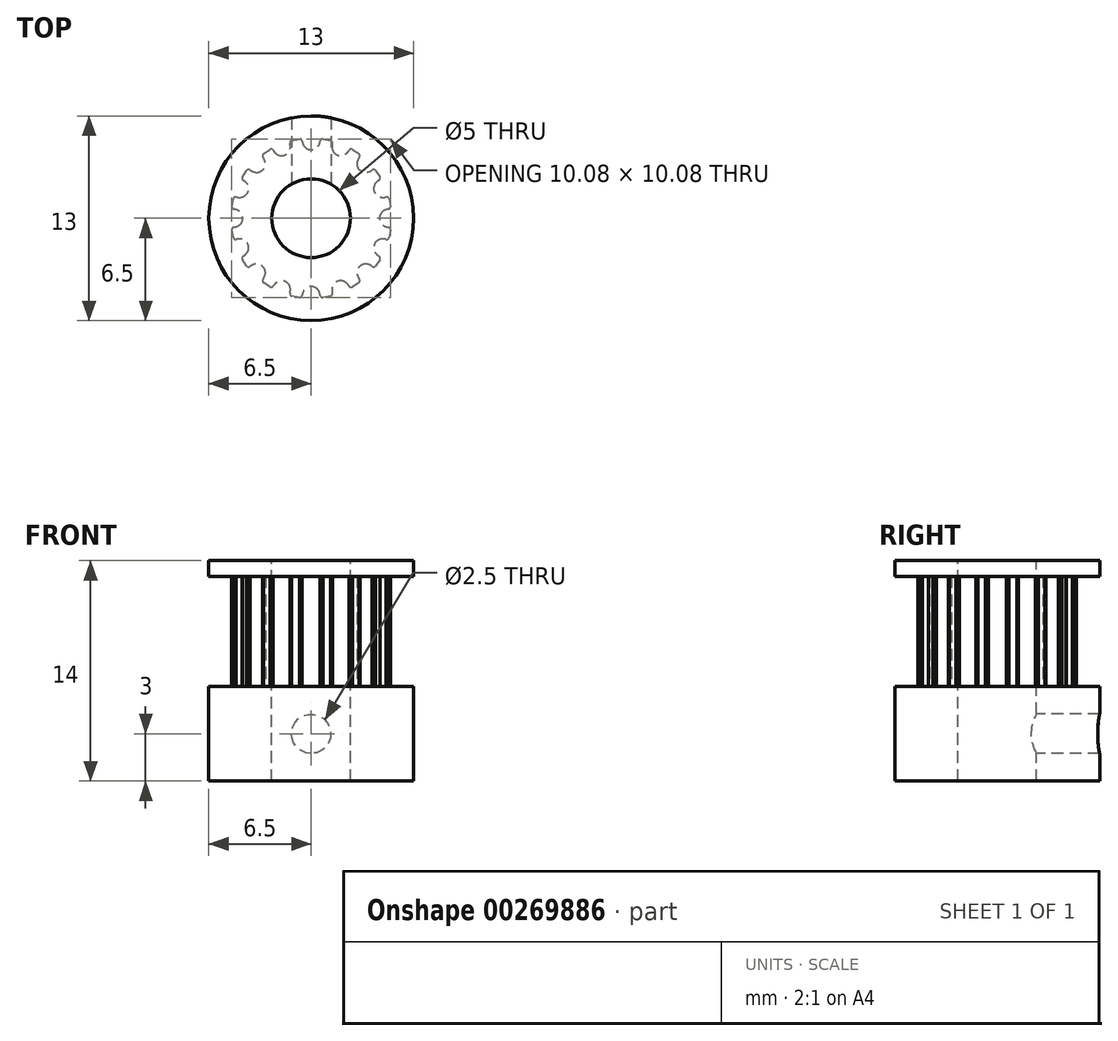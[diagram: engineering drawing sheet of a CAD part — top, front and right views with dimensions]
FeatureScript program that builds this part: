
annotation { "Feature Type Name" : "Feature", "Feature Type Description" : "" }
export const myFeature = defineFeature(function(context is Context, id is Id, definition is map)
    precondition{}
    {
        {
            var Q0;
            Q0=qCreatedBy(makeId("Top.planeOp"),FACE);
            var sketch = newSketch(context, id + "F0", { "sketchPlane" : qUnion([Q0])});
            skLineSegment(sketch, "E0", {"start": v(0, 0) * mm, "end": v(8.05, 0) * mm, "construction": true});
            skArc(sketch, "E1", {"start": v(5.1, 0) * mm, "mid": v(5, 1) * mm, "end": v(4.7, 1.95) * mm, "construction": true});
            skLineSegment(sketch, "E2", {"start": v(0, 0) * mm, "end": v(4.7, 1.95) * mm, "construction": true});
            skPoint(sketch, "E3", {"position": v(4.34, 0) * mm});
            skPoint(sketch, "E4", {"position": v(4.9, 0) * mm});
            skArc(sketch, "E5", {"start": v(4.68, 0.5) * mm, "mid": v(4.34, 0) * mm, "end": v(4.68, -0.5) * mm});
            skArc(sketch, "E6", {"start": v(4.9, 0.58) * mm, "mid": v(4.79, 0.55) * mm, "end": v(4.68, 0.5) * mm});
            skArc(sketch, "E7", {"start": v(4.94, 0) * mm, "mid": v(4.85, 0.96) * mm, "end": v(4.57, 1.9) * mm, "construction": true});
            skArc(sketch, "E8", {"start": v(4.9, 0.58) * mm, "mid": v(5, 0.64) * mm, "end": v(5.04, 0.75) * mm});
            skArc(sketch, "E9", {"start": v(4.97, -1.1) * mm, "mid": v(5.06, -0.56) * mm, "end": v(5.1, 0) * mm, "construction": true});
            skLineSegment(sketch, "E10", {"start": v(0, 0) * mm, "end": v(5, 1) * mm, "construction": true});
            skPoint(sketch, "E11", {"position": v(5, 1) * mm});
            skArc(sketch, "E12.MirrorCS", {"start": v(4.76, 1.34) * mm, "mid": v(4.87, 1.33) * mm, "end": v(4.94, 1.24) * mm});
            skArc(sketch, "E13.MirrorCS", {"start": v(4.76, 1.34) * mm, "mid": v(4.64, 1.32) * mm, "end": v(4.51, 1.32) * mm});
            skArc(sketch, "E14.MirrorCS", {"start": v(4.51, 1.32) * mm, "mid": v(4.01, 1.66) * mm, "end": v(4.12, 2.26) * mm});
            skLineSegment(sketch, "E15", {"start": v(4.94, 1.24) * mm, "end": v(5.04, 0.75) * mm});
            skArc(sketch, "E16.1.0", {"start": v(4.12, 2.26) * mm, "mid": v(4.01, 1.66) * mm, "end": v(4.51, 1.32) * mm});
            skArc(sketch, "E16.1.1", {"start": v(4.31, 2.41) * mm, "mid": v(4.21, 2.34) * mm, "end": v(4.12, 2.26) * mm});
            skArc(sketch, "E16.1.2", {"start": v(4.31, 2.41) * mm, "mid": v(4.38, 2.5) * mm, "end": v(4.37, 2.62) * mm});
            skLineSegment(sketch, "E16.1.3", {"start": v(4.1, 3.03) * mm, "end": v(4.37, 2.62) * mm});
            skArc(sketch, "E16.1.4", {"start": v(3.88, 3.06) * mm, "mid": v(4, 3.1) * mm, "end": v(4.1, 3.03) * mm});
            skArc(sketch, "E16.1.5", {"start": v(3.88, 3.06) * mm, "mid": v(3.78, 3) * mm, "end": v(3.67, 2.95) * mm});
            skArc(sketch, "E16.2.0", {"start": v(2.95, 3.67) * mm, "mid": v(3.07, 3.07) * mm, "end": v(3.67, 2.95) * mm});
            skArc(sketch, "E16.2.1", {"start": v(3.06, 3.88) * mm, "mid": v(3, 3.78) * mm, "end": v(2.95, 3.67) * mm});
            skArc(sketch, "E16.2.2", {"start": v(3.06, 3.88) * mm, "mid": v(3.1, 4) * mm, "end": v(3.03, 4.1) * mm});
            skLineSegment(sketch, "E16.2.3", {"start": v(2.62, 4.37) * mm, "end": v(3.03, 4.1) * mm});
            skArc(sketch, "E16.2.4", {"start": v(2.41, 4.31) * mm, "mid": v(2.5, 4.38) * mm, "end": v(2.62, 4.37) * mm});
            skArc(sketch, "E16.2.5", {"start": v(2.41, 4.31) * mm, "mid": v(2.34, 4.21) * mm, "end": v(2.26, 4.12) * mm});
            skArc(sketch, "E16.3.0", {"start": v(1.32, 4.51) * mm, "mid": v(1.66, 4.01) * mm, "end": v(2.26, 4.12) * mm});
            skArc(sketch, "E16.3.1", {"start": v(1.34, 4.76) * mm, "mid": v(1.32, 4.64) * mm, "end": v(1.32, 4.51) * mm});
            skArc(sketch, "E16.3.2", {"start": v(1.34, 4.76) * mm, "mid": v(1.33, 4.87) * mm, "end": v(1.24, 4.94) * mm});
            skLineSegment(sketch, "E16.3.3", {"start": v(0.75, 5.04) * mm, "end": v(1.24, 4.94) * mm});
            skArc(sketch, "E16.3.4", {"start": v(0.58, 4.9) * mm, "mid": v(0.64, 5) * mm, "end": v(0.75, 5.04) * mm});
            skArc(sketch, "E16.3.5", {"start": v(0.58, 4.9) * mm, "mid": v(0.55, 4.79) * mm, "end": v(0.5, 4.68) * mm});
            skArc(sketch, "E16.4.0", {"start": v(-0.5, 4.68) * mm, "mid": v(0, 4.34) * mm, "end": v(0.5, 4.68) * mm});
            skArc(sketch, "E16.4.1", {"start": v(-0.58, 4.9) * mm, "mid": v(-0.55, 4.79) * mm, "end": v(-0.5, 4.68) * mm});
            skArc(sketch, "E16.4.2", {"start": v(-0.58, 4.9) * mm, "mid": v(-0.64, 5) * mm, "end": v(-0.75, 5.04) * mm});
            skLineSegment(sketch, "E16.4.3", {"start": v(-1.24, 4.94) * mm, "end": v(-0.75, 5.04) * mm});
            skArc(sketch, "E16.4.4", {"start": v(-1.34, 4.76) * mm, "mid": v(-1.33, 4.87) * mm, "end": v(-1.24, 4.94) * mm});
            skArc(sketch, "E16.4.5", {"start": v(-1.34, 4.76) * mm, "mid": v(-1.32, 4.64) * mm, "end": v(-1.32, 4.51) * mm});
            skArc(sketch, "E16.5.0", {"start": v(-2.26, 4.12) * mm, "mid": v(-1.66, 4.01) * mm, "end": v(-1.32, 4.51) * mm});
            skArc(sketch, "E16.5.1", {"start": v(-2.41, 4.31) * mm, "mid": v(-2.34, 4.21) * mm, "end": v(-2.26, 4.12) * mm});
            skArc(sketch, "E16.5.2", {"start": v(-2.41, 4.31) * mm, "mid": v(-2.5, 4.38) * mm, "end": v(-2.62, 4.37) * mm});
            skLineSegment(sketch, "E16.5.3", {"start": v(-3.03, 4.1) * mm, "end": v(-2.62, 4.37) * mm});
            skArc(sketch, "E16.5.4", {"start": v(-3.06, 3.88) * mm, "mid": v(-3.1, 4) * mm, "end": v(-3.03, 4.1) * mm});
            skArc(sketch, "E16.5.5", {"start": v(-3.06, 3.88) * mm, "mid": v(-3, 3.78) * mm, "end": v(-2.95, 3.67) * mm});
            skArc(sketch, "E16.6.0", {"start": v(-3.67, 2.95) * mm, "mid": v(-3.07, 3.07) * mm, "end": v(-2.95, 3.67) * mm});
            skArc(sketch, "E16.6.1", {"start": v(-3.88, 3.06) * mm, "mid": v(-3.78, 3) * mm, "end": v(-3.67, 2.95) * mm});
            skArc(sketch, "E16.6.2", {"start": v(-3.88, 3.06) * mm, "mid": v(-4, 3.1) * mm, "end": v(-4.1, 3.03) * mm});
            skLineSegment(sketch, "E16.6.3", {"start": v(-4.37, 2.62) * mm, "end": v(-4.1, 3.03) * mm});
            skArc(sketch, "E16.6.4", {"start": v(-4.31, 2.41) * mm, "mid": v(-4.38, 2.5) * mm, "end": v(-4.37, 2.62) * mm});
            skArc(sketch, "E16.6.5", {"start": v(-4.31, 2.41) * mm, "mid": v(-4.21, 2.34) * mm, "end": v(-4.12, 2.26) * mm});
            skArc(sketch, "E16.7.0", {"start": v(-4.51, 1.32) * mm, "mid": v(-4.01, 1.66) * mm, "end": v(-4.12, 2.26) * mm});
            skArc(sketch, "E16.7.1", {"start": v(-4.76, 1.34) * mm, "mid": v(-4.64, 1.32) * mm, "end": v(-4.51, 1.32) * mm});
            skArc(sketch, "E16.7.2", {"start": v(-4.76, 1.34) * mm, "mid": v(-4.87, 1.33) * mm, "end": v(-4.94, 1.24) * mm});
            skLineSegment(sketch, "E16.7.3", {"start": v(-5.04, 0.75) * mm, "end": v(-4.94, 1.24) * mm});
            skArc(sketch, "E16.7.4", {"start": v(-4.9, 0.58) * mm, "mid": v(-5, 0.64) * mm, "end": v(-5.04, 0.75) * mm});
            skArc(sketch, "E16.7.5", {"start": v(-4.9, 0.58) * mm, "mid": v(-4.79, 0.55) * mm, "end": v(-4.68, 0.5) * mm});
            skArc(sketch, "E16.8.0", {"start": v(-4.68, -0.5) * mm, "mid": v(-4.34, 0) * mm, "end": v(-4.68, 0.5) * mm});
            skArc(sketch, "E16.8.1", {"start": v(-4.9, -0.58) * mm, "mid": v(-4.79, -0.55) * mm, "end": v(-4.68, -0.5) * mm});
            skArc(sketch, "E16.8.2", {"start": v(-4.9, -0.58) * mm, "mid": v(-5, -0.64) * mm, "end": v(-5.04, -0.75) * mm});
            skLineSegment(sketch, "E16.8.3", {"start": v(-4.94, -1.24) * mm, "end": v(-5.04, -0.75) * mm});
            skArc(sketch, "E16.8.4", {"start": v(-4.76, -1.34) * mm, "mid": v(-4.87, -1.33) * mm, "end": v(-4.94, -1.24) * mm});
            skArc(sketch, "E16.8.5", {"start": v(-4.76, -1.34) * mm, "mid": v(-4.64, -1.32) * mm, "end": v(-4.51, -1.32) * mm});
            skArc(sketch, "E16.9.0", {"start": v(-4.12, -2.26) * mm, "mid": v(-4.01, -1.66) * mm, "end": v(-4.51, -1.32) * mm});
            skArc(sketch, "E16.9.1", {"start": v(-4.31, -2.41) * mm, "mid": v(-4.21, -2.34) * mm, "end": v(-4.12, -2.26) * mm});
            skArc(sketch, "E16.9.2", {"start": v(-4.31, -2.41) * mm, "mid": v(-4.38, -2.5) * mm, "end": v(-4.37, -2.62) * mm});
            skLineSegment(sketch, "E16.9.3", {"start": v(-4.1, -3.03) * mm, "end": v(-4.37, -2.62) * mm});
            skArc(sketch, "E16.9.4", {"start": v(-3.88, -3.06) * mm, "mid": v(-4, -3.1) * mm, "end": v(-4.1, -3.03) * mm});
            skArc(sketch, "E16.9.5", {"start": v(-3.88, -3.06) * mm, "mid": v(-3.78, -3) * mm, "end": v(-3.67, -2.95) * mm});
            skArc(sketch, "E16.10.0", {"start": v(-2.95, -3.67) * mm, "mid": v(-3.07, -3.07) * mm, "end": v(-3.67, -2.95) * mm});
            skArc(sketch, "E16.10.1", {"start": v(-3.06, -3.88) * mm, "mid": v(-3, -3.78) * mm, "end": v(-2.95, -3.67) * mm});
            skArc(sketch, "E16.10.2", {"start": v(-3.06, -3.88) * mm, "mid": v(-3.1, -4) * mm, "end": v(-3.03, -4.1) * mm});
            skLineSegment(sketch, "E16.10.3", {"start": v(-2.62, -4.37) * mm, "end": v(-3.03, -4.1) * mm});
            skArc(sketch, "E16.10.4", {"start": v(-2.41, -4.31) * mm, "mid": v(-2.5, -4.38) * mm, "end": v(-2.62, -4.37) * mm});
            skArc(sketch, "E16.10.5", {"start": v(-2.41, -4.31) * mm, "mid": v(-2.34, -4.21) * mm, "end": v(-2.26, -4.12) * mm});
            skArc(sketch, "E16.11.0", {"start": v(-1.32, -4.51) * mm, "mid": v(-1.66, -4.01) * mm, "end": v(-2.26, -4.12) * mm});
            skArc(sketch, "E16.11.1", {"start": v(-1.34, -4.76) * mm, "mid": v(-1.32, -4.64) * mm, "end": v(-1.32, -4.51) * mm});
            skArc(sketch, "E16.11.2", {"start": v(-1.34, -4.76) * mm, "mid": v(-1.33, -4.87) * mm, "end": v(-1.24, -4.94) * mm});
            skLineSegment(sketch, "E16.11.3", {"start": v(-0.75, -5.04) * mm, "end": v(-1.24, -4.94) * mm});
            skArc(sketch, "E16.11.4", {"start": v(-0.58, -4.9) * mm, "mid": v(-0.64, -5) * mm, "end": v(-0.75, -5.04) * mm});
            skArc(sketch, "E16.11.5", {"start": v(-0.58, -4.9) * mm, "mid": v(-0.55, -4.79) * mm, "end": v(-0.5, -4.68) * mm});
            skArc(sketch, "E16.12.0", {"start": v(0.5, -4.68) * mm, "mid": v(0, -4.34) * mm, "end": v(-0.5, -4.68) * mm});
            skArc(sketch, "E16.12.1", {"start": v(0.58, -4.9) * mm, "mid": v(0.55, -4.79) * mm, "end": v(0.5, -4.68) * mm});
            skArc(sketch, "E16.12.2", {"start": v(0.58, -4.9) * mm, "mid": v(0.64, -5) * mm, "end": v(0.75, -5.04) * mm});
            skLineSegment(sketch, "E16.12.3", {"start": v(1.24, -4.94) * mm, "end": v(0.75, -5.04) * mm});
            skArc(sketch, "E16.12.4", {"start": v(1.34, -4.76) * mm, "mid": v(1.33, -4.87) * mm, "end": v(1.24, -4.94) * mm});
            skArc(sketch, "E16.12.5", {"start": v(1.34, -4.76) * mm, "mid": v(1.32, -4.64) * mm, "end": v(1.32, -4.51) * mm});
            skArc(sketch, "E16.13.0", {"start": v(2.26, -4.12) * mm, "mid": v(1.66, -4.01) * mm, "end": v(1.32, -4.51) * mm});
            skArc(sketch, "E16.13.1", {"start": v(2.41, -4.31) * mm, "mid": v(2.34, -4.21) * mm, "end": v(2.26, -4.12) * mm});
            skArc(sketch, "E16.13.2", {"start": v(2.41, -4.31) * mm, "mid": v(2.5, -4.38) * mm, "end": v(2.62, -4.37) * mm});
            skLineSegment(sketch, "E16.13.3", {"start": v(3.03, -4.1) * mm, "end": v(2.62, -4.37) * mm});
            skArc(sketch, "E16.13.4", {"start": v(3.06, -3.88) * mm, "mid": v(3.1, -4) * mm, "end": v(3.03, -4.1) * mm});
            skArc(sketch, "E16.13.5", {"start": v(3.06, -3.88) * mm, "mid": v(3, -3.78) * mm, "end": v(2.95, -3.67) * mm});
            skArc(sketch, "E16.14.0", {"start": v(3.67, -2.95) * mm, "mid": v(3.07, -3.07) * mm, "end": v(2.95, -3.67) * mm});
            skArc(sketch, "E16.14.1", {"start": v(3.88, -3.06) * mm, "mid": v(3.78, -3) * mm, "end": v(3.67, -2.95) * mm});
            skArc(sketch, "E16.14.2", {"start": v(3.88, -3.06) * mm, "mid": v(4, -3.1) * mm, "end": v(4.1, -3.03) * mm});
            skLineSegment(sketch, "E16.14.3", {"start": v(4.37, -2.62) * mm, "end": v(4.1, -3.03) * mm});
            skArc(sketch, "E16.14.4", {"start": v(4.31, -2.41) * mm, "mid": v(4.38, -2.5) * mm, "end": v(4.37, -2.62) * mm});
            skArc(sketch, "E16.14.5", {"start": v(4.31, -2.41) * mm, "mid": v(4.21, -2.34) * mm, "end": v(4.12, -2.26) * mm});
            skArc(sketch, "E16.15.0", {"start": v(4.51, -1.32) * mm, "mid": v(4.01, -1.66) * mm, "end": v(4.12, -2.26) * mm});
            skArc(sketch, "E16.15.1", {"start": v(4.76, -1.34) * mm, "mid": v(4.64, -1.32) * mm, "end": v(4.51, -1.32) * mm});
            skArc(sketch, "E16.15.2", {"start": v(4.76, -1.34) * mm, "mid": v(4.87, -1.33) * mm, "end": v(4.94, -1.24) * mm});
            skLineSegment(sketch, "E16.15.3", {"start": v(5.04, -0.75) * mm, "end": v(4.94, -1.24) * mm});
            skArc(sketch, "E16.15.4", {"start": v(4.9, -0.58) * mm, "mid": v(5, -0.64) * mm, "end": v(5.04, -0.75) * mm});
            skArc(sketch, "E16.15.5", {"start": v(4.9, -0.58) * mm, "mid": v(4.79, -0.55) * mm, "end": v(4.68, -0.5) * mm});
            skCircle(sketch, "E17", {"center": v(0, 0) * mm, "radius": 2.5 * mm});
            skCircle(sketch, "E18", {"center": v(0, 0) * mm, "radius": 6.5 * mm});
            skSolve(sketch);
        }
        {
            var Q0;
            Q0=makeQuery(id+"F0.imprint","IMPRINT",FACE,{"disambiguationData":[TD([[makeQuery(id+"F0.imprint","IMPRINT",EDGE,{"derivedFrom":sQuery(id+"F0.wireOp",EDGE,"E5")}),-1.0]])]});
            var Q1;
            Q1=makeQuery(id+"F0.imprint","IMPRINT",FACE,{"disambiguationData":[TD([[makeQuery(id+"F0.imprint","IMPRINT",EDGE,{"derivedFrom":sQuery(id+"F0.wireOp",EDGE,"E5")}),1.0]])]});
            extrude(context, id + "F1", {"entities" : qUnion([Q0, Q1]), "oppositeDirection" : true, "depth" : 6 * mm});
        }
        {
            var Q0;
            Q0=makeQuery(id+"F0.imprint","IMPRINT",FACE,{"disambiguationData":[TD([[makeQuery(id+"F0.imprint","IMPRINT",EDGE,{"derivedFrom":sQuery(id+"F0.wireOp",EDGE,"E5")}),-1.0]])]});
            extrude(context, id + "F2", {"entities" : qUnion([Q0]), "operationType" : NewBodyOperationType.ADD, "depth" : 7 * mm});
        }
        {
            var Q0;
            Q0=makeQuery(id+"F0.imprint","IMPRINT",FACE,{"disambiguationData":[TD([[makeQuery(id+"F0.imprint","IMPRINT",EDGE,{"derivedFrom":sQuery(id+"F0.wireOp",EDGE,"E5")}),1.0]])]});
            var Q1;
            Q1=makeQuery(id+"F0.imprint","IMPRINT",FACE,{"disambiguationData":[TD([[makeQuery(id+"F0.imprint","IMPRINT",EDGE,{"derivedFrom":sQuery(id+"F0.wireOp",EDGE,"E5")}),-1.0]])]});
            var Q2;
            Q2=makeQuery(id+"F2.opExtrude","CAP_FACE",FACE,{"disambiguationData":[OSD([sQuery(id+"F0.wireOp",EDGE,"E5"),sQuery(id+"F0.wireOp",EDGE,"E6"),sQuery(id+"F0.wireOp",EDGE,"E8"),sQuery(id+"F0.wireOp",EDGE,"E12.MirrorCS"),sQuery(id+"F0.wireOp",EDGE,"E13.MirrorCS"),sQuery(id+"F0.wireOp",EDGE,"E15"),sQuery(id+"F0.wireOp",EDGE,"E16.1.0"),sQuery(id+"F0.wireOp",EDGE,"E16.1.1"),sQuery(id+"F0.wireOp",EDGE,"E16.1.2"),sQuery(id+"F0.wireOp",EDGE,"E16.1.3"),sQuery(id+"F0.wireOp",EDGE,"E16.1.4"),sQuery(id+"F0.wireOp",EDGE,"E16.1.5"),sQuery(id+"F0.wireOp",EDGE,"E16.2.0"),sQuery(id+"F0.wireOp",EDGE,"E16.2.1"),sQuery(id+"F0.wireOp",EDGE,"E16.2.2"),sQuery(id+"F0.wireOp",EDGE,"E16.2.3"),sQuery(id+"F0.wireOp",EDGE,"E16.2.4"),sQuery(id+"F0.wireOp",EDGE,"E16.2.5"),sQuery(id+"F0.wireOp",EDGE,"E16.3.0"),sQuery(id+"F0.wireOp",EDGE,"E16.3.1"),sQuery(id+"F0.wireOp",EDGE,"E16.3.2"),sQuery(id+"F0.wireOp",EDGE,"E16.3.3"),sQuery(id+"F0.wireOp",EDGE,"E16.3.4"),sQuery(id+"F0.wireOp",EDGE,"E16.3.5"),sQuery(id+"F0.wireOp",EDGE,"E16.4.0"),sQuery(id+"F0.wireOp",EDGE,"E16.4.1"),sQuery(id+"F0.wireOp",EDGE,"E16.4.2"),sQuery(id+"F0.wireOp",EDGE,"E16.4.3"),sQuery(id+"F0.wireOp",EDGE,"E16.4.4"),sQuery(id+"F0.wireOp",EDGE,"E16.4.5"),sQuery(id+"F0.wireOp",EDGE,"E16.5.0"),sQuery(id+"F0.wireOp",EDGE,"E16.5.1"),sQuery(id+"F0.wireOp",EDGE,"E16.5.2"),sQuery(id+"F0.wireOp",EDGE,"E16.5.3"),sQuery(id+"F0.wireOp",EDGE,"E16.5.4"),sQuery(id+"F0.wireOp",EDGE,"E16.5.5"),sQuery(id+"F0.wireOp",EDGE,"E16.6.0"),sQuery(id+"F0.wireOp",EDGE,"E16.6.1"),sQuery(id+"F0.wireOp",EDGE,"E16.6.2"),sQuery(id+"F0.wireOp",EDGE,"E16.6.3"),sQuery(id+"F0.wireOp",EDGE,"E16.6.4"),sQuery(id+"F0.wireOp",EDGE,"E16.6.5"),sQuery(id+"F0.wireOp",EDGE,"E16.7.0"),sQuery(id+"F0.wireOp",EDGE,"E16.7.1"),sQuery(id+"F0.wireOp",EDGE,"E16.7.2"),sQuery(id+"F0.wireOp",EDGE,"E16.7.3"),sQuery(id+"F0.wireOp",EDGE,"E16.7.4"),sQuery(id+"F0.wireOp",EDGE,"E16.7.5"),sQuery(id+"F0.wireOp",EDGE,"E16.8.0"),sQuery(id+"F0.wireOp",EDGE,"E16.8.1"),sQuery(id+"F0.wireOp",EDGE,"E16.8.2"),sQuery(id+"F0.wireOp",EDGE,"E16.8.3"),sQuery(id+"F0.wireOp",EDGE,"E16.8.4"),sQuery(id+"F0.wireOp",EDGE,"E16.8.5"),sQuery(id+"F0.wireOp",EDGE,"E16.9.0"),sQuery(id+"F0.wireOp",EDGE,"E16.9.1"),sQuery(id+"F0.wireOp",EDGE,"E16.9.2"),sQuery(id+"F0.wireOp",EDGE,"E16.9.3"),sQuery(id+"F0.wireOp",EDGE,"E16.9.4"),sQuery(id+"F0.wireOp",EDGE,"E16.9.5"),sQuery(id+"F0.wireOp",EDGE,"E16.10.0"),sQuery(id+"F0.wireOp",EDGE,"E16.10.1"),sQuery(id+"F0.wireOp",EDGE,"E16.10.2"),sQuery(id+"F0.wireOp",EDGE,"E16.10.3"),sQuery(id+"F0.wireOp",EDGE,"E16.10.4"),sQuery(id+"F0.wireOp",EDGE,"E16.10.5"),sQuery(id+"F0.wireOp",EDGE,"E16.11.0"),sQuery(id+"F0.wireOp",EDGE,"E16.11.1"),sQuery(id+"F0.wireOp",EDGE,"E16.11.2"),sQuery(id+"F0.wireOp",EDGE,"E16.11.3"),sQuery(id+"F0.wireOp",EDGE,"E16.11.4"),sQuery(id+"F0.wireOp",EDGE,"E16.11.5"),sQuery(id+"F0.wireOp",EDGE,"E16.12.0"),sQuery(id+"F0.wireOp",EDGE,"E16.12.1"),sQuery(id+"F0.wireOp",EDGE,"E16.12.2"),sQuery(id+"F0.wireOp",EDGE,"E16.12.3"),sQuery(id+"F0.wireOp",EDGE,"E16.12.4"),sQuery(id+"F0.wireOp",EDGE,"E16.12.5"),sQuery(id+"F0.wireOp",EDGE,"E16.13.0"),sQuery(id+"F0.wireOp",EDGE,"E16.13.1"),sQuery(id+"F0.wireOp",EDGE,"E16.13.2"),sQuery(id+"F0.wireOp",EDGE,"E16.13.3"),sQuery(id+"F0.wireOp",EDGE,"E16.13.4"),sQuery(id+"F0.wireOp",EDGE,"E16.13.5"),sQuery(id+"F0.wireOp",EDGE,"E16.14.0"),sQuery(id+"F0.wireOp",EDGE,"E16.14.1"),sQuery(id+"F0.wireOp",EDGE,"E16.14.2"),sQuery(id+"F0.wireOp",EDGE,"E16.14.3"),sQuery(id+"F0.wireOp",EDGE,"E16.14.4"),sQuery(id+"F0.wireOp",EDGE,"E16.14.5"),sQuery(id+"F0.wireOp",EDGE,"E16.15.0"),sQuery(id+"F0.wireOp",EDGE,"E16.15.1"),sQuery(id+"F0.wireOp",EDGE,"E16.15.2"),sQuery(id+"F0.wireOp",EDGE,"E16.15.3"),sQuery(id+"F0.wireOp",EDGE,"E16.15.4"),sQuery(id+"F0.wireOp",EDGE,"E16.15.5"),sQuery(id+"F0.wireOp",EDGE,"E17")])],"isStart":false});
            var Q3;
            Q3=makeQuery(id+"F2.opExtrude","CAP_FACE",FACE,{"disambiguationData":[OSD([sQuery(id+"F0.wireOp",EDGE,"E5"),sQuery(id+"F0.wireOp",EDGE,"E6"),sQuery(id+"F0.wireOp",EDGE,"E8"),sQuery(id+"F0.wireOp",EDGE,"E12.MirrorCS"),sQuery(id+"F0.wireOp",EDGE,"E13.MirrorCS"),sQuery(id+"F0.wireOp",EDGE,"E15"),sQuery(id+"F0.wireOp",EDGE,"E16.1.0"),sQuery(id+"F0.wireOp",EDGE,"E16.1.1"),sQuery(id+"F0.wireOp",EDGE,"E16.1.2"),sQuery(id+"F0.wireOp",EDGE,"E16.1.3"),sQuery(id+"F0.wireOp",EDGE,"E16.1.4"),sQuery(id+"F0.wireOp",EDGE,"E16.1.5"),sQuery(id+"F0.wireOp",EDGE,"E16.2.0"),sQuery(id+"F0.wireOp",EDGE,"E16.2.1"),sQuery(id+"F0.wireOp",EDGE,"E16.2.2"),sQuery(id+"F0.wireOp",EDGE,"E16.2.3"),sQuery(id+"F0.wireOp",EDGE,"E16.2.4"),sQuery(id+"F0.wireOp",EDGE,"E16.2.5"),sQuery(id+"F0.wireOp",EDGE,"E16.3.0"),sQuery(id+"F0.wireOp",EDGE,"E16.3.1"),sQuery(id+"F0.wireOp",EDGE,"E16.3.2"),sQuery(id+"F0.wireOp",EDGE,"E16.3.3"),sQuery(id+"F0.wireOp",EDGE,"E16.3.4"),sQuery(id+"F0.wireOp",EDGE,"E16.3.5"),sQuery(id+"F0.wireOp",EDGE,"E16.4.0"),sQuery(id+"F0.wireOp",EDGE,"E16.4.1"),sQuery(id+"F0.wireOp",EDGE,"E16.4.2"),sQuery(id+"F0.wireOp",EDGE,"E16.4.3"),sQuery(id+"F0.wireOp",EDGE,"E16.4.4"),sQuery(id+"F0.wireOp",EDGE,"E16.4.5"),sQuery(id+"F0.wireOp",EDGE,"E16.5.0"),sQuery(id+"F0.wireOp",EDGE,"E16.5.1"),sQuery(id+"F0.wireOp",EDGE,"E16.5.2"),sQuery(id+"F0.wireOp",EDGE,"E16.5.3"),sQuery(id+"F0.wireOp",EDGE,"E16.5.4"),sQuery(id+"F0.wireOp",EDGE,"E16.5.5"),sQuery(id+"F0.wireOp",EDGE,"E16.6.0"),sQuery(id+"F0.wireOp",EDGE,"E16.6.1"),sQuery(id+"F0.wireOp",EDGE,"E16.6.2"),sQuery(id+"F0.wireOp",EDGE,"E16.6.3"),sQuery(id+"F0.wireOp",EDGE,"E16.6.4"),sQuery(id+"F0.wireOp",EDGE,"E16.6.5"),sQuery(id+"F0.wireOp",EDGE,"E16.7.0"),sQuery(id+"F0.wireOp",EDGE,"E16.7.1"),sQuery(id+"F0.wireOp",EDGE,"E16.7.2"),sQuery(id+"F0.wireOp",EDGE,"E16.7.3"),sQuery(id+"F0.wireOp",EDGE,"E16.7.4"),sQuery(id+"F0.wireOp",EDGE,"E16.7.5"),sQuery(id+"F0.wireOp",EDGE,"E16.8.0"),sQuery(id+"F0.wireOp",EDGE,"E16.8.1"),sQuery(id+"F0.wireOp",EDGE,"E16.8.2"),sQuery(id+"F0.wireOp",EDGE,"E16.8.3"),sQuery(id+"F0.wireOp",EDGE,"E16.8.4"),sQuery(id+"F0.wireOp",EDGE,"E16.8.5"),sQuery(id+"F0.wireOp",EDGE,"E16.9.0"),sQuery(id+"F0.wireOp",EDGE,"E16.9.1"),sQuery(id+"F0.wireOp",EDGE,"E16.9.2"),sQuery(id+"F0.wireOp",EDGE,"E16.9.3"),sQuery(id+"F0.wireOp",EDGE,"E16.9.4"),sQuery(id+"F0.wireOp",EDGE,"E16.9.5"),sQuery(id+"F0.wireOp",EDGE,"E16.10.0"),sQuery(id+"F0.wireOp",EDGE,"E16.10.1"),sQuery(id+"F0.wireOp",EDGE,"E16.10.2"),sQuery(id+"F0.wireOp",EDGE,"E16.10.3"),sQuery(id+"F0.wireOp",EDGE,"E16.10.4"),sQuery(id+"F0.wireOp",EDGE,"E16.10.5"),sQuery(id+"F0.wireOp",EDGE,"E16.11.0"),sQuery(id+"F0.wireOp",EDGE,"E16.11.1"),sQuery(id+"F0.wireOp",EDGE,"E16.11.2"),sQuery(id+"F0.wireOp",EDGE,"E16.11.3"),sQuery(id+"F0.wireOp",EDGE,"E16.11.4"),sQuery(id+"F0.wireOp",EDGE,"E16.11.5"),sQuery(id+"F0.wireOp",EDGE,"E16.12.0"),sQuery(id+"F0.wireOp",EDGE,"E16.12.1"),sQuery(id+"F0.wireOp",EDGE,"E16.12.2"),sQuery(id+"F0.wireOp",EDGE,"E16.12.3"),sQuery(id+"F0.wireOp",EDGE,"E16.12.4"),sQuery(id+"F0.wireOp",EDGE,"E16.12.5"),sQuery(id+"F0.wireOp",EDGE,"E16.13.0"),sQuery(id+"F0.wireOp",EDGE,"E16.13.1"),sQuery(id+"F0.wireOp",EDGE,"E16.13.2"),sQuery(id+"F0.wireOp",EDGE,"E16.13.3"),sQuery(id+"F0.wireOp",EDGE,"E16.13.4"),sQuery(id+"F0.wireOp",EDGE,"E16.13.5"),sQuery(id+"F0.wireOp",EDGE,"E16.14.0"),sQuery(id+"F0.wireOp",EDGE,"E16.14.1"),sQuery(id+"F0.wireOp",EDGE,"E16.14.2"),sQuery(id+"F0.wireOp",EDGE,"E16.14.3"),sQuery(id+"F0.wireOp",EDGE,"E16.14.4"),sQuery(id+"F0.wireOp",EDGE,"E16.14.5"),sQuery(id+"F0.wireOp",EDGE,"E16.15.0"),sQuery(id+"F0.wireOp",EDGE,"E16.15.1"),sQuery(id+"F0.wireOp",EDGE,"E16.15.2"),sQuery(id+"F0.wireOp",EDGE,"E16.15.3"),sQuery(id+"F0.wireOp",EDGE,"E16.15.4"),sQuery(id+"F0.wireOp",EDGE,"E16.15.5"),sQuery(id+"F0.wireOp",EDGE,"E17")])],"isStart":false});
            extrude(context, id + "F3", {"entities" : qUnion([Q0, Q1]), "operationType" : NewBodyOperationType.ADD, "endBoundEntityFace" : qUnion([Q2]), "depth" : 8 * mm, "hasSecondDirection" : true, "secondDirectionBound" : SecondDirectionBoundingType.UP_TO_SURFACE, "secondDirectionOppositeDirection" : false, "secondDirectionBoundEntityFace" : qUnion([Q3]), "secondDirectionDepth" : 8 * mm});
        }
        {
            var Q0;
            Q0=qCreatedBy(makeId("Front.planeOp"),FACE);
            var sketch = newSketch(context, id + "F4", { "sketchPlane" : qUnion([Q0])});
            skLineSegment(sketch, "E19", {"start": v(0, 0) * mm, "end": v(-6.5, 0) * mm, "construction": true});
            skLineSegment(sketch, "E20", {"start": v(-6.5, 0) * mm, "end": v(-6.5, -6) * mm, "construction": true});
            skLineSegment(sketch, "E21", {"start": v(-6.5, -6) * mm, "end": v(6.5, -6) * mm, "construction": true});
            skLineSegment(sketch, "E22", {"start": v(6.5, -6) * mm, "end": v(6.5, 0) * mm, "construction": true});
            skLineSegment(sketch, "E23", {"start": v(6.5, 0) * mm, "end": v(0, 0) * mm, "construction": true});
            skPoint(sketch, "E24", {"position": v(-6.5, -3) * mm});
            skPoint(sketch, "E25", {"position": v(0, -3) * mm});
            skCircle(sketch, "E26", {"center": v(0, -3) * mm, "radius": 1.25 * mm});
            skSolve(sketch);
        }
        {
            var Q0;
            Q0=qSketchRegion(id+"F4",true);
            extrude(context, id + "F5", {"entities" : qUnion([Q0]), "operationType" : NewBodyOperationType.REMOVE, "oppositeDirection" : true, "depth" : 25 * mm});
        }
        {
            var Q0;
            Q0=makeQuery(id+"F1.opExtrude","SWEPT_BODY",BODY,{"disambiguationData":[OSD([sQuery(id+"F0.wireOp",EDGE,"E17"),sQuery(id+"F0.wireOp",EDGE,"E18")])]});
            transform(context, id + "F6", {"entities" : qUnion([Q0]), "transformType" : TransformType.TRANSLATION_3D, "dx" : 0 * mm, "dy" : 0 * mm, "dz" : 8 * mm, "makeCopy" : false});
        }
    });
